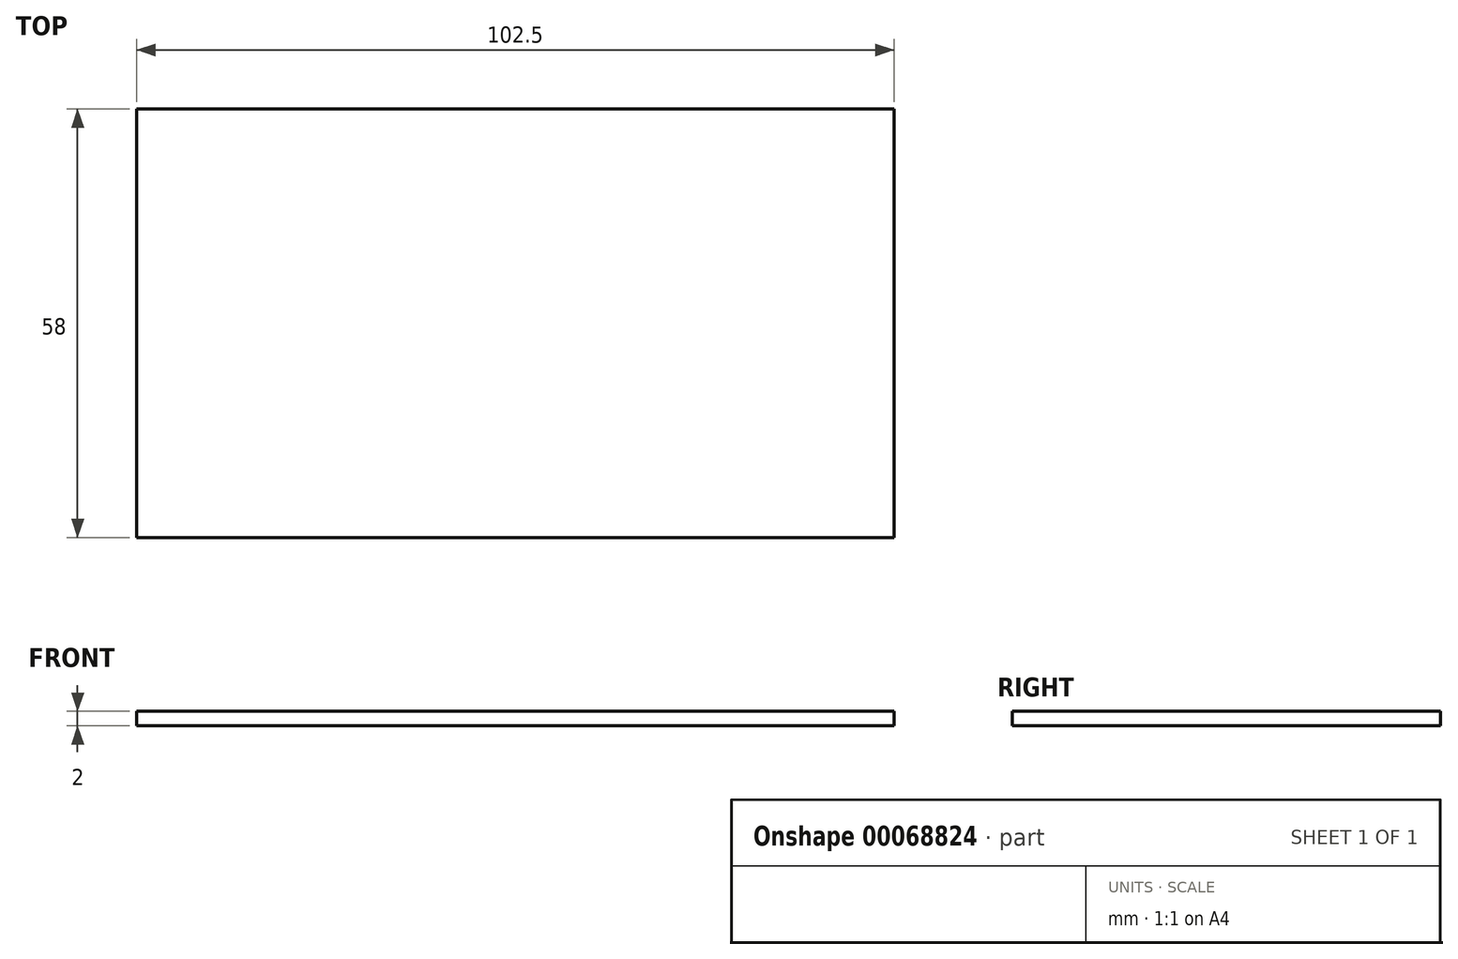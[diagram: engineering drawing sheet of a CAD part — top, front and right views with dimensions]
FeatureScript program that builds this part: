
annotation { "Feature Type Name" : "Feature", "Feature Type Description" : "" }
export const myFeature = defineFeature(function(context is Context, id is Id, definition is map)
    precondition{}
    {
        {
            var Q0;
            Q0=qCreatedBy(makeId("Top.planeOp"),FACE);
            var sketch = newSketch(context, id + "F0", { "sketchPlane" : qUnion([Q0])});
            skLineSegment(sketch, "E0.bottom", {"start": v(0, 0) * mm, "end": v(102.5, 0) * mm});
            skLineSegment(sketch, "E0.top", {"start": v(0, -58) * mm, "end": v(102.5, -58) * mm});
            skLineSegment(sketch, "E0.left", {"start": v(0, 0) * mm, "end": v(0, -58) * mm});
            skLineSegment(sketch, "E0.right", {"start": v(102.5, 0) * mm, "end": v(102.5, -58) * mm});
            skSolve(sketch);
        }
        {
            var Q0;
            Q0 = qSketchRegion(id + "F0", true);
            extrude(context, id + "F1", {"entities" : qUnion([Q0]), "depth" : 2 * mm});
        }
    });
